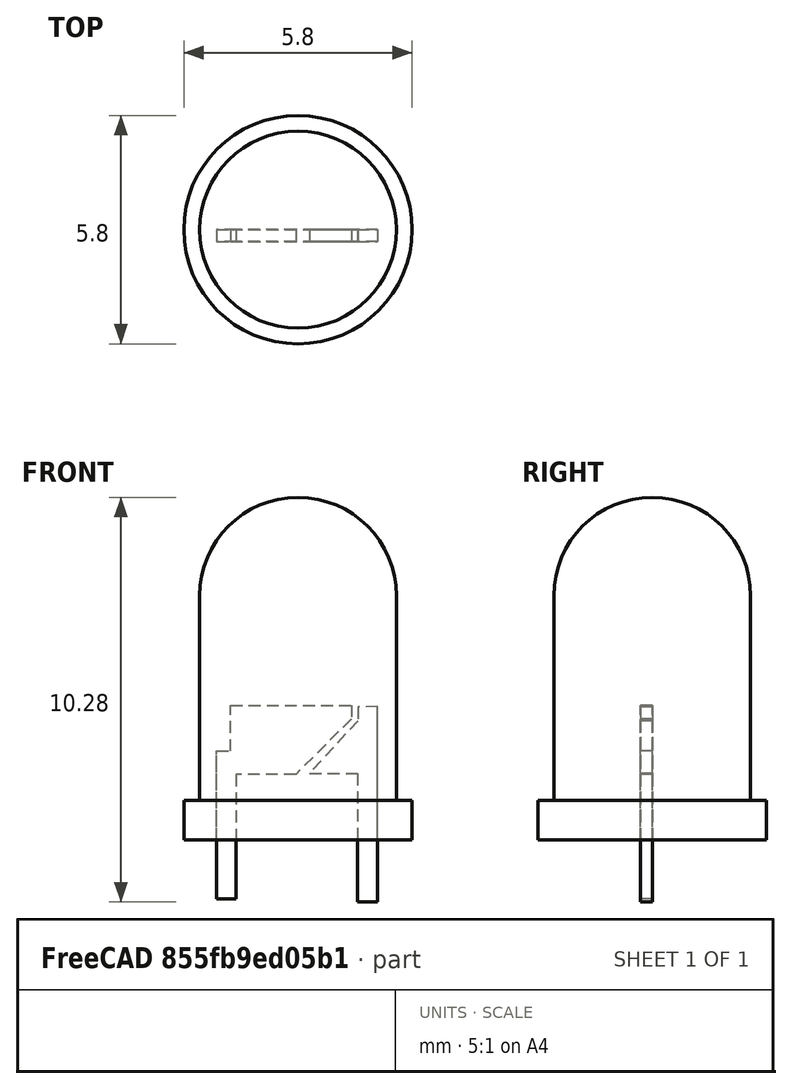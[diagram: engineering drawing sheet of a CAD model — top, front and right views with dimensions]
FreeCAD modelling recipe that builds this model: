
FCSTD DOCUMENT  (FreeCAD 0.16R6703 (Git))
Label: led-5mm
License: CC-BY 3.0
LicenseURL: http://creativecommons.org/licenses/by/3.0/
objects: Part::Cylinder×2, Sketcher::SketchObject×2, PartDesign::Pad×2, Part::Sphere×1, Part::MultiFuse×1
note: 10 computed .brp shape members not serialized (recipe doc carries the construction recipe); baked Part::Feature solids carry a one-line shape summary decoded from their .brp

FEATURE [Part::Cylinder] Cylinder  label="Cilindro"
  Angle = 360
  Height = 6.2
  Radius = 2.5
FEATURE [Part::Sphere] Sphere  label="Esféra"
  Angle1 = -90
  Angle2 = 90
  Angle3 = 180
  Placement = pos=(0,0,6.2) rot=(1,0,0;1.5708rad)
  Radius = 2.5
FEATURE [Part::Cylinder] Cylinder001  label="Cilindro001"
  Angle = 360
  Height = 1
  Radius = 2.9
FEATURE [Part::MultiFuse] Fusion  label="Funda"
  Shapes = -> [Cylinder,Cylinder001,Sphere]
FEATURE [Sketcher::SketchObject] Sketch
  Placement = pos=(0,0,0) rot=(1,0,0;1.5708rad)
  sketch-geometry (9):
    g0: LineSegment StartX=-2.06901 StartY=-1.50757 StartZ=0 EndX=-2.06901 EndY=2.25482 EndZ=0
    g1: LineSegment StartX=-2.06901 StartY=2.25482 StartZ=0 EndX=-1.71216 EndY=2.25482 EndZ=0
    g2: LineSegment StartX=-1.71216 StartY=2.25482 StartZ=0 EndX=-1.71216 EndY=3.41819 EndZ=0
    g3: LineSegment StartX=-1.71216 StartY=3.41819 StartZ=0 EndX=1.35716 EndY=3.41819 EndZ=0
    g4: LineSegment StartX=1.35716 StartY=3.41819 StartZ=0 EndX=1.35716 EndY=3.07166 EndZ=0
    g5: LineSegment StartX=1.35716 StartY=3.07166 StartZ=0 EndX=-0.05374 EndY=1.66076 EndZ=0
    g6: LineSegment StartX=-0.05374 StartY=1.66076 StartZ=0 EndX=-1.56901 EndY=1.66076 EndZ=0
    g7: LineSegment StartX=-1.56901 StartY=1.66076 StartZ=0 EndX=-1.56901 EndY=-1.5 EndZ=0
    g8: LineSegment StartX=-1.56901 StartY=-1.5 StartZ=0 EndX=-2.06901 EndY=-1.50757 EndZ=0
  constraints (18):
    c: Vertical(g0)
    c: Coincident(g0,g1)
    c: Horizontal(g1)
    c: Coincident(g1,g2)
    c: Vertical(g2)
    c: Coincident(g2,g3)
    c: Horizontal(g3)
    c: Coincident(g3,g4)
    c: Vertical(g4)
    c: Coincident(g4,g5)
    c: Coincident(g5,g6)
    c: Horizontal(g6)
    c: Coincident(g6,g7)
    c: Vertical(g7)
    c: Coincident(g7,g8)
    c: Coincident(g8,g0)
    c: DistanceY(g-1,g7) = -1.5
    c: DistanceX(g0,g7) = 0.5
FEATURE [PartDesign::Pad] Pad  label="Catodo"
  Length = 0.3
  Length2 = 100
  Placement = pos=(0,0,0) rot=(1,0,0;1.5708rad)
  Sketch = -> Sketch
  Type = 0
FEATURE [Sketcher::SketchObject] Sketch001
  Placement = pos=(0,0,0) rot=(1,0,0;1.5708rad)
  sketch-geometry (7):
    g0: LineSegment StartX=2.0234 StartY=-1.57582 StartZ=0 EndX=2.0234 EndY=3.38927 EndZ=0
    g1: LineSegment StartX=2.0234 StartY=3.38927 StartZ=0 EndX=1.5234 EndY=3.36901 EndZ=0
    g2: LineSegment StartX=1.5234 StartY=3.36901 StartZ=0 EndX=1.5234 EndY=3.02449 EndZ=0
    g3: LineSegment StartX=1.5234 StartY=3.02449 StartZ=0 EndX=0.294592 EndY=1.68695 EndZ=0
    g4: LineSegment StartX=0.294592 StartY=1.68695 StartZ=0 EndX=1.51053 EndY=1.68695 EndZ=0
    g5: LineSegment StartX=1.51053 StartY=1.68695 StartZ=0 EndX=1.51053 EndY=-1.57582 EndZ=0
    g6: LineSegment StartX=1.51053 StartY=-1.57582 StartZ=0 EndX=2.0234 EndY=-1.57582 EndZ=0
  constraints (13):
    c: Vertical(g0)
    c: Coincident(g1,g0)
    c: DistanceX(g1,g0) = 0.5
    c: Coincident(g1,g2)
    c: Vertical(g2)
    c: Coincident(g2,g3)
    c: Coincident(g3,g4)
    c: Horizontal(g4)
    c: Coincident(g4,g5)
    c: Vertical(g5)
    c: Coincident(g5,g6)
    c: Coincident(g6,g0)
    c: Horizontal(g6)
FEATURE [PartDesign::Pad] Pad001  label="Anodo"
  Length = 0.3
  Length2 = 100
  Placement = pos=(0,0,0) rot=(1,0,0;1.5708rad)
  Sketch = -> Sketch001
  Type = 0
